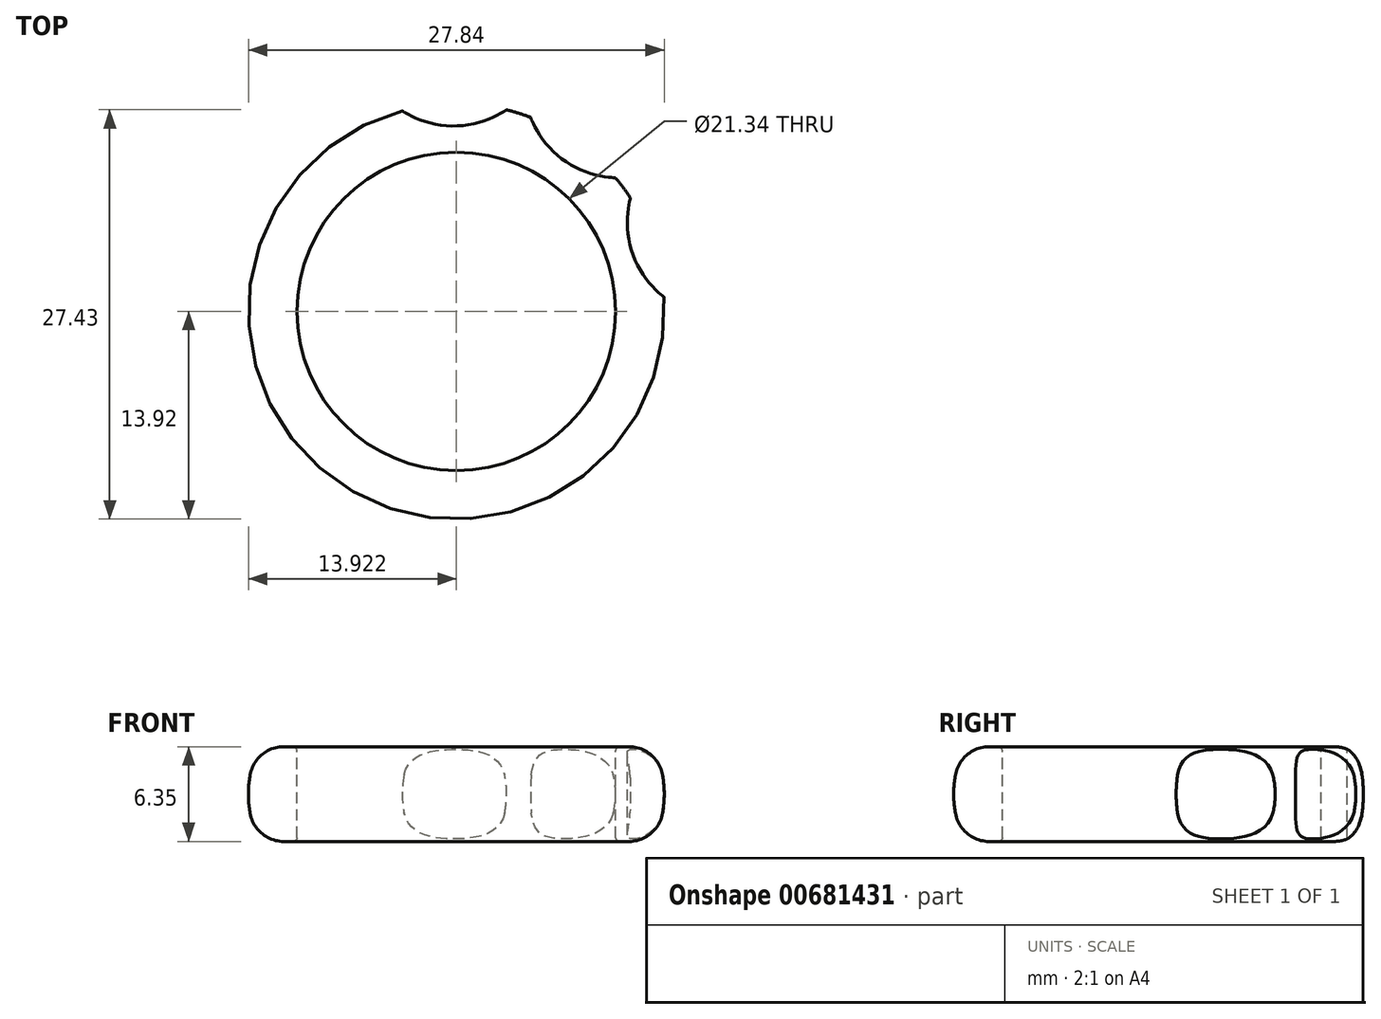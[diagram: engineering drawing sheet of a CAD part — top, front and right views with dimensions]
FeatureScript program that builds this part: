
annotation { "Feature Type Name" : "Feature", "Feature Type Description" : "" }
export const myFeature = defineFeature(function(context is Context, id is Id, definition is map)
    precondition{}
    {
        {
            var Q0;
            Q0=qCreatedBy(makeId("Front.planeOp"),FACE);
            var sketch = newSketch(context, id + "F0", { "sketchPlane" : qUnion([Q0])});
            skLineSegment(sketch, "E0", {"start": v(0, 0) * mm, "end": v(0, -6.35) * mm});
            skLineSegment(sketch, "E1", {"start": v(0, 0) * mm, "end": v(2.54, 0) * mm});
            skLineSegment(sketch, "E2", {"start": v(0, -6.35) * mm, "end": v(2.54, -6.35) * mm});
            skLineSegment(sketch, "E3", {"start": v(-10.67, -3.18) * mm, "end": v(-10.67, -7.09) * mm});
            skPoint(sketch, "E3.startSnap0", {"position": v(0, -3.18) * mm});
            skArc(sketch, "E4", {"start": v(2.54, -6.35) * mm, "mid": v(3.25, -3.17) * mm, "end": v(2.54, 0) * mm});
            skSolve(sketch);
        }
        {
            var Q0;
            Q0=makeQuery(id+"F0.imprint","IMPRINT",FACE,{"disambiguationData":[TD([[makeQuery(id+"F0.imprint","IMPRINT",EDGE,{"derivedFrom":sQuery(id+"F0.wireOp",EDGE,"E0")}),1.0]])]});
            var Q1;
            Q1=sQuery(id+"F0.wireOp",EDGE,"E3");
            revolve(context, id + "F1", {"entities" : qUnion([Q0]), "axis" : qUnion([Q1]), "revolveType" : RevolveType.FULL});
        }
        {
            var Q0;
            Q0=makeQuery(id+"F1.opRevolve","SWEPT_EDGE",EDGE,{"disambiguationData":[OSD([sQuery(id+"F0.wireOp",EDGE,"E1"),sQuery(id+"F0.wireOp",EDGE,"E4")])]});
            var Q1;
            Q1=makeQuery(id+"F1.opRevolve","SWEPT_EDGE",EDGE,{"disambiguationData":[OSD([sQuery(id+"F0.wireOp",EDGE,"E2"),sQuery(id+"F0.wireOp",EDGE,"E4")])]});
            fillet(context, id + "F2", {"entities" : qUnion([Q0, Q1]), "radius" : 2.3 * mm, "tangentPropagation" : true, "allowEdgeOverflow" : false});
        }
        {
            var Q0;
            Q0=makeQuery(id+"F1.opRevolve","SWEPT_FACE",FACE,{"disambiguationData":[OSD([sQuery(id+"F0.wireOp",EDGE,"E0")])]});
            fillet(context, id + "F3", {"entities" : qUnion([Q0]), "radius" : 0.25 * mm, "tangentPropagation" : true, "allowEdgeOverflow" : false});
        }
        {
            var Q0;
            Q0=qCreatedBy(makeId("Top.planeOp"),FACE);
            var sketch = newSketch(context, id + "F4", { "sketchPlane" : qUnion([Q0])});
            skArc(sketch, "E5.0", {"start": v(-30.14, 11.78) * mm, "mid": v(-29.2, 13.2) * mm, "end": v(-28.18, 14.54) * mm});
            skCircle(sketch, "E6", {"center": v(-10.67, 0) * mm, "radius": 18.78 * mm});
            skCircle(sketch, "E7", {"center": v(-10.85, 18.78) * mm, "radius": 6.35 * mm});
            skCircle(sketch, "E8.1.1", {"center": v(-21.85, 15.08) * mm, "radius": 6.35 * mm});
            skCircle(sketch, "E8.2.1", {"center": v(-28.58, 5.63) * mm, "radius": 6.35 * mm});
            skCircle(sketch, "E9.2.3.0", {"center": v(-28.47, -5.98) * mm, "radius": 6.35 * mm});
            skCircle(sketch, "E9.2.4.0", {"center": v(-21.56, -15.3) * mm, "radius": 6.35 * mm});
            skCircle(sketch, "E9.2.5.0", {"center": v(-10.49, -18.78) * mm, "radius": 6.35 * mm});
            skCircle(sketch, "E10.2.6.0", {"center": v(0.52, -15.08) * mm, "radius": 6.35 * mm});
            skCircle(sketch, "E10.2.7.0", {"center": v(7.25, -5.63) * mm, "radius": 6.35 * mm});
            skCircle(sketch, "E10.2.8.0", {"center": v(7.13, 5.98) * mm, "radius": 6.35 * mm});
            skCircle(sketch, "E10.2.9.0", {"center": v(0.22, 15.3) * mm, "radius": 6.35 * mm});
            skArc(sketch, "E11.trimOffspring", {"start": v(-19.5, 20.98) * mm, "mid": v(7.87, -13.2) * mm, "end": v(-33.38, 1.47) * mm});
            skSolve(sketch);
        }
        {
            var Q0;
            {var subQ0=sQuery(id+"F4.wireOp",EDGE,"E6");var subQ1=sQuery(id+"F4.wireOp",EDGE,"E8.1.1");var subQ2=makeQuery(id+"F4.imprint","INTERSECT",VERTEX,{"disambiguationData":[OD(0.0)],"derivedFrom":[subQ1,subQ0]});Q0=makeQuery(id+"F4.imprint","IMPRINT",FACE,{"disambiguationData":[TD([[makeQuery(id+"F4.imprint","IMPRINT",EDGE,{"disambiguationData":[TD([[subQ2,-1.0]])],"derivedFrom":subQ1}),-1.0]])]});}
            var Q1;
            {var subQ0=sQuery(id+"F4.wireOp",EDGE,"E6");var subQ1=sQuery(id+"F4.wireOp",EDGE,"E8.2.1");var subQ2=makeQuery(id+"F4.imprint","INTERSECT",VERTEX,{"disambiguationData":[OD(0.0)],"derivedFrom":[subQ1,subQ0]});Q1=makeQuery(id+"F4.imprint","IMPRINT",FACE,{"disambiguationData":[TD([[makeQuery(id+"F4.imprint","IMPRINT",EDGE,{"disambiguationData":[TD([[subQ2,-1.0]])],"derivedFrom":subQ1}),-1.0]])]});}
            var Q2;
            {var subQ0=sQuery(id+"F4.wireOp",EDGE,"E6");var subQ1=sQuery(id+"F4.wireOp",EDGE,"E9.2.3.0");var subQ2=makeQuery(id+"F4.imprint","INTERSECT",VERTEX,{"disambiguationData":[OD(0.0)],"derivedFrom":[subQ1,subQ0]});Q2=makeQuery(id+"F4.imprint","IMPRINT",FACE,{"disambiguationData":[TD([[makeQuery(id+"F4.imprint","IMPRINT",EDGE,{"disambiguationData":[TD([[subQ2,-1.0]])],"derivedFrom":subQ1}),-1.0]])]});}
            var Q3;
            {var subQ0=sQuery(id+"F4.wireOp",EDGE,"E6");var subQ1=sQuery(id+"F4.wireOp",EDGE,"E9.2.4.0");var subQ2=makeQuery(id+"F4.imprint","INTERSECT",VERTEX,{"disambiguationData":[OD(0.0)],"derivedFrom":[subQ1,subQ0]});Q3=makeQuery(id+"F4.imprint","IMPRINT",FACE,{"disambiguationData":[TD([[makeQuery(id+"F4.imprint","IMPRINT",EDGE,{"disambiguationData":[TD([[subQ2,-1.0]])],"derivedFrom":subQ1}),-1.0]])]});}
            var Q4;
            {var subQ0=sQuery(id+"F4.wireOp",EDGE,"E6");var subQ1=sQuery(id+"F4.wireOp",EDGE,"E9.2.5.0");var subQ2=makeQuery(id+"F4.imprint","INTERSECT",VERTEX,{"disambiguationData":[OD(0.0)],"derivedFrom":[subQ1,subQ0]});Q4=makeQuery(id+"F4.imprint","IMPRINT",FACE,{"disambiguationData":[TD([[makeQuery(id+"F4.imprint","IMPRINT",EDGE,{"disambiguationData":[TD([[subQ2,-1.0]])],"derivedFrom":subQ1}),-1.0]])]});}
            var Q5;
            {var subQ0=sQuery(id+"F4.wireOp",EDGE,"E6");var subQ1=sQuery(id+"F4.wireOp",EDGE,"E10.2.6.0");var subQ2=makeQuery(id+"F4.imprint","INTERSECT",VERTEX,{"disambiguationData":[OD(0.0)],"derivedFrom":[subQ1,subQ0]});Q5=makeQuery(id+"F4.imprint","IMPRINT",FACE,{"disambiguationData":[TD([[makeQuery(id+"F4.imprint","IMPRINT",EDGE,{"disambiguationData":[TD([[subQ2,-1.0]])],"derivedFrom":subQ1}),-1.0]])]});}
            var Q6;
            {var subQ0=sQuery(id+"F4.wireOp",EDGE,"E6");var subQ1=sQuery(id+"F4.wireOp",EDGE,"E10.2.7.0");var subQ2=makeQuery(id+"F4.imprint","INTERSECT",VERTEX,{"disambiguationData":[OD(0.0)],"derivedFrom":[subQ1,subQ0]});Q6=makeQuery(id+"F4.imprint","IMPRINT",FACE,{"disambiguationData":[TD([[makeQuery(id+"F4.imprint","IMPRINT",EDGE,{"disambiguationData":[TD([[subQ2,-1.0]])],"derivedFrom":subQ1}),-1.0]])]});}
            var Q7;
            {var subQ0=sQuery(id+"F4.wireOp",EDGE,"E10.2.9.0");var subQ1=sQuery(id+"F4.wireOp",EDGE,"E7");var subQ2=makeQuery(id+"F4.imprint","INTERSECT",VERTEX,{"disambiguationData":[OD(1.0)],"derivedFrom":[subQ1,subQ0]});Q7=makeQuery(id+"F4.imprint","IMPRINT",FACE,{"disambiguationData":[TD([[makeQuery(id+"F4.imprint","IMPRINT",EDGE,{"disambiguationData":[TD([[subQ2,-1.0]])],"derivedFrom":subQ1}),-1.0]])]});}
            var Q8;
            {var subQ0=sQuery(id+"F4.wireOp",EDGE,"E8.1.1");var subQ1=sQuery(id+"F4.wireOp",EDGE,"E7");var subQ2=makeQuery(id+"F4.imprint","INTERSECT",VERTEX,{"disambiguationData":[OD(1.0)],"derivedFrom":[subQ1,subQ0]});Q8=makeQuery(id+"F4.imprint","IMPRINT",FACE,{"disambiguationData":[TD([[makeQuery(id+"F4.imprint","IMPRINT",EDGE,{"disambiguationData":[TD([[subQ2,-1.0]])],"derivedFrom":subQ1}),1.0]])]});}
            var Q9;
            {var subQ0=sQuery(id+"F4.wireOp",EDGE,"E6");var subQ1=sQuery(id+"F4.wireOp",EDGE,"E7");var subQ2=makeQuery(id+"F4.imprint","INTERSECT",VERTEX,{"disambiguationData":[OD(0.0)],"derivedFrom":[subQ1,subQ0]});Q9=makeQuery(id+"F4.imprint","IMPRINT",FACE,{"disambiguationData":[TD([[makeQuery(id+"F4.imprint","IMPRINT",EDGE,{"disambiguationData":[TD([[subQ2,-1.0]])],"derivedFrom":subQ1}),-1.0]])]});}
            extrude(context, id + "F5", {"entities" : qUnion([Q0, Q1, Q2, Q3, Q4, Q5, Q6, Q7, Q8, Q9]), "operationType" : NewBodyOperationType.REMOVE, "oppositeDirection" : true, "depth" : 40.03 * mm, "offsetDistance" : 25.4 * mm});
        }
    });
